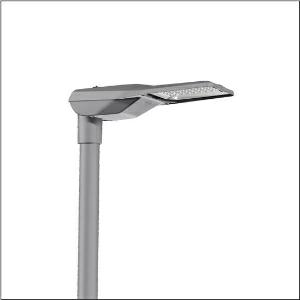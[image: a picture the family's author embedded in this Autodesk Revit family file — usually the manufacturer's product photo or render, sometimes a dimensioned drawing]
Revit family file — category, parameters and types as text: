
# Revit family: streetlight_sl_21_mini___p0_8ab_5xe2r33s08gb_ab20
name_source: partatom
category: Lighting Fixtures
units: mm (PartAtom-declared; Revit-internal decimal feet)

## family parameters
Cut with Voids When Loaded = No
Host = Face
Light Source = No
Part Type = Normal
Room Calculation Point = No
Round Connector Dimension = Use Diameter
Shared = No

## types (1)
- --- (1 x LED, 5160 lm, 40.4 W, 3000K)
    Apparent Load = 40 VA
    CIE Flux Codes = 36 71 98 100 100
    Color Rendering = 70
    Color Temperature = 3000K
    Default Elevation = 1800 mm
    Description = Streetlight SL 21 mini, mast luminaire, primary light control with lens, of PMMA, primary optical cover: cover, of toughened safety glass, transparent, light distribution: P0.8aB, light emission: direct distribution, primary light characteristic: asymmetric, installation type: post-top, side-entry, LED, High Power LED, rated luminous flux: 5.160lm, luminous efficacy: 128lm/W, light colour: 730, colour temperature: 3000K, control gear: D4i, control: pre-setting: logarithmic dimming characteristic, flexible luminous flux parameterisation, time-dependent luminous flux control, constant luminous flux control, overheat protection, mains connection: 220..240V, AC, 50/60Hz, start of lifetime: 40W, end of service life: 41W, reduction: 19W, luminaire housing, of diecast aluminium, powder-coated, SITECO metallic grey (DB 702S), corrosivity category C5 high according to DIN EN ISO 12944, multi-level sealing system, sealing non-destructively replaceable, inclination adjustable: 0°, 5°, 10°, 15°, please order mast flange separately, length: 628mm, width: 235mm, height: 110mm, mast flange for spigot size: 42mm (side-entry): 5XC10008XM4, 60/48mm (side-entry/post-top): 5XC10108XM2, 76/60mm (side-entry/post-top): 5XC10108XM1, mounting height: 4..8m, Smart Interface above, protection rating (complete): IP66, insulation class (complete): insulation class II (safety insulation), certification: CE, ENEC, ENEC+, VDE, impact resistance: IK10, permissible operating ambient temperature for outdoor applications: -40..+50°C, standard-compliant lighting for roads and squares, packaging unit: 1 piece

Light Distribution: P0.8aB
    Height = 110 mm
    Lamp = 1 x LED
    Lamp Light Flux = 5160 lm
    Lamp Power = 40.4 W
    Lamp count = 1
    Length = 625 mm
    Luminous efficacy = 128 lm/W
    Manufacturer = Siteco
    ModVariant = No
    Model = 5XE2R33S08GB
    Mounting Place = Pole
    Mounting Type = Pole top
    Number of Poles = 1
    OnlyDefault = Yes
    Power Factor = 1
    Product Name = Streetlight SL 21 mini | P0.8aB
    Product group = mast luminaire | pylon top
    ProductGroupID = 6100
    Protection Class = Protection class II
    Protection Degree = IP 66
    RLX_Detail_Level = 1
    RLX_Emergency_Light_Flux = 0 lm
    RLX_Emergency_Type = 0
    RLX_Emergency_Type_DB = No
    RlxData = <blob elided: 91833 chars, md5=916147c8>
    Socket = socket
    Standby Power = 0 W
    System Light Flux = 5160 lm
    System Power = 40 W
    Type Comments = factory setting: luminous flux: 100 % | dim-lin: 254 | 812 mA
    Type Image = l_1003515.jpg
    URL = http://relux.com
    VarID = @adj_083939
    Voltage = 0 V
    Weight = 0.00 kg
    Width = 234 mm

## geometry (parser evidence)
native form markers: Blend x4, Sweep x11
no freeform markers — native parametric forms only
